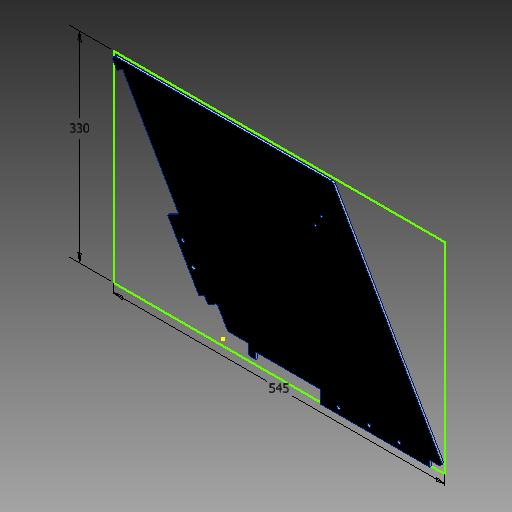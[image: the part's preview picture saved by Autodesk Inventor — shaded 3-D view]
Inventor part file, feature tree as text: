
AUTODESK INVENTOR PART (.ipt)
format: ipt  version: 2019.4 (Build 234330000, 330)  size: 227,328 bytes
history: native  units: mm
features: sketch x7, extrude x6, fillet x4
ambient origin geometry x8: Origin, YZ Plane, XZ Plane, XY Plane, X Axis, Y Axis, Z Axis, Center Point
bodies: Body1 (feature_tree)
feature tree (17):
  extrude  "Extrusion6"  Depth=3.0mm TaperAngle=0.0deg
  extrude  "Extrusion7"  TaperAngle=120.0deg  [1 undecoded]
  extrude  "Extrusion8"  Depth=3.0mm
  fillet  "Fillet1"  [1 undecoded]
  fillet  "Fillet2"  Radius=35.0mm
  fillet  "Fillet3"  Radius=3.0mm
  fillet  "Fillet4"  Radius=100.0mm
  extrude  "Extrusion12"  TaperAngle=30.0deg  [1 undecoded]
  extrude  "Extrusion13"  TaperAngle=60.0deg  [1 undecoded]
  extrude  "Extrusion14"  TaperAngle=30.0deg  [1 undecoded]
  sketch  "Sketch16"  dims[d76=3.5mm d77=20.0mm d78=90.0deg d79=3.5mm d80=3.0mm d81=0.0mm d82=5.0mm d83=2.0mm d84=2.0mm d85=2.0mm d123=10.0mm d124=103.0mm d125=120.0deg d126=10.0mm d127=115.0mm d128=180.0mm d129=10.0mm d130=3.0mm d131=0.0mm d132=0.0mm d133=184.0mm d134=11.0mm d135=9.0mm d136=106.0mm d137=11.0mm d138=3.0mm d139=0.0mm d140=50.0mm d141=5.5mm d142=30.0mm d144=50.0mm d145=10.0mm d147=10.0mm d149=35.0mm d150=120.0deg d151=5.5mm d152=20.0mm d154=35.0mm d155=10.0mm d157=10.0mm d159=3.0mm d160=0.0mm d161=545.0mm d162=330.0mm]
  sketch  "Sketch7"  dims[d56=365.0mm d58=3.0mm d59=0.0mm]
  sketch  "Sketch8"  dims[d60=90.0mm d61=120.0deg]
  sketch  "Sketch9"  dims[d62=35.0mm d63=90.0mm d64=0.0mm d65=35.0mm d66=3.0mm d67=0.0mm d69=100.0mm]
  sketch  "Sketch13"  dims[d70=90.0deg d71=30.0deg]
  sketch  "Sketch14"  dims[d72=305.0mm d73=60.0deg]
  sketch  "Sketch15"  dims[d74=13.0mm d75=30.0deg]
note: 5 required parameter values undecoded (feature->parameter linkage not recoverable at this tier; creation-order binding heuristic only, values carry confidence <= 0.55)
